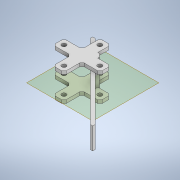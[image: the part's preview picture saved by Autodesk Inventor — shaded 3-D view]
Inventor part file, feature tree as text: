
AUTODESK INVENTOR PART (.ipt)
format: ipt  version: 2020 (Build 240168000, 168)  size: 234,496 bytes
history: native  units: mm
features: extrude x3, chamfer x3, sketch x3, plane x1, mirror x1
ambient origin geometry x8: Origin, YZ Plane, XZ Plane, XY Plane, X Axis, Y Axis, Z Axis, Center Point
bodies: Solid1 (feature_tree)
feature tree (11):
  extrude  "Extrusion1"  Depth=4.0mm
  chamfer  "Chamfer1"  Distance=4.0mm
  extrude  "Extrusion2"  Depth=2.0mm
  plane  "Work Plane1"
  mirror  "Mirror1"
  chamfer  "Chamfer2"  Distance=16.5mm
  extrude  "Extrusion3"  Depth=16.5mm
  chamfer  "Chamfer3"  Distance=3.0mm
  sketch  "Sketch1"  dims[d0=4.0mm d1=4.0mm]
  sketch  "Sketch3"  dims[d2=16.5mm]
  sketch  "Sketch4"  dims[d3=16.5mm d4=4.0mm d5=4.0mm d6=16.5mm d7=16.5mm d8=3.0mm d9=10.0mm d10=3.0mm d11=3.0mm d12=5.0mm d13=5.0mm d14=5.0mm d15=5.0mm d16=3.0mm d17=0.0mm d18=2.0mm d19=2.0mm d20=45.0deg d25=0.0mm d26=3.0mm d27=25.0mm d28=75.0mm d29=10.0mm d30=0.0mm d31=0.0mm d32=1.5mm d33=2.0mm d34=45.0deg d35=5.0mm d36=5.0mm d37=3.0mm d38=0.0mm d39=3.0mm d40=2.0mm d41=45.0deg]
